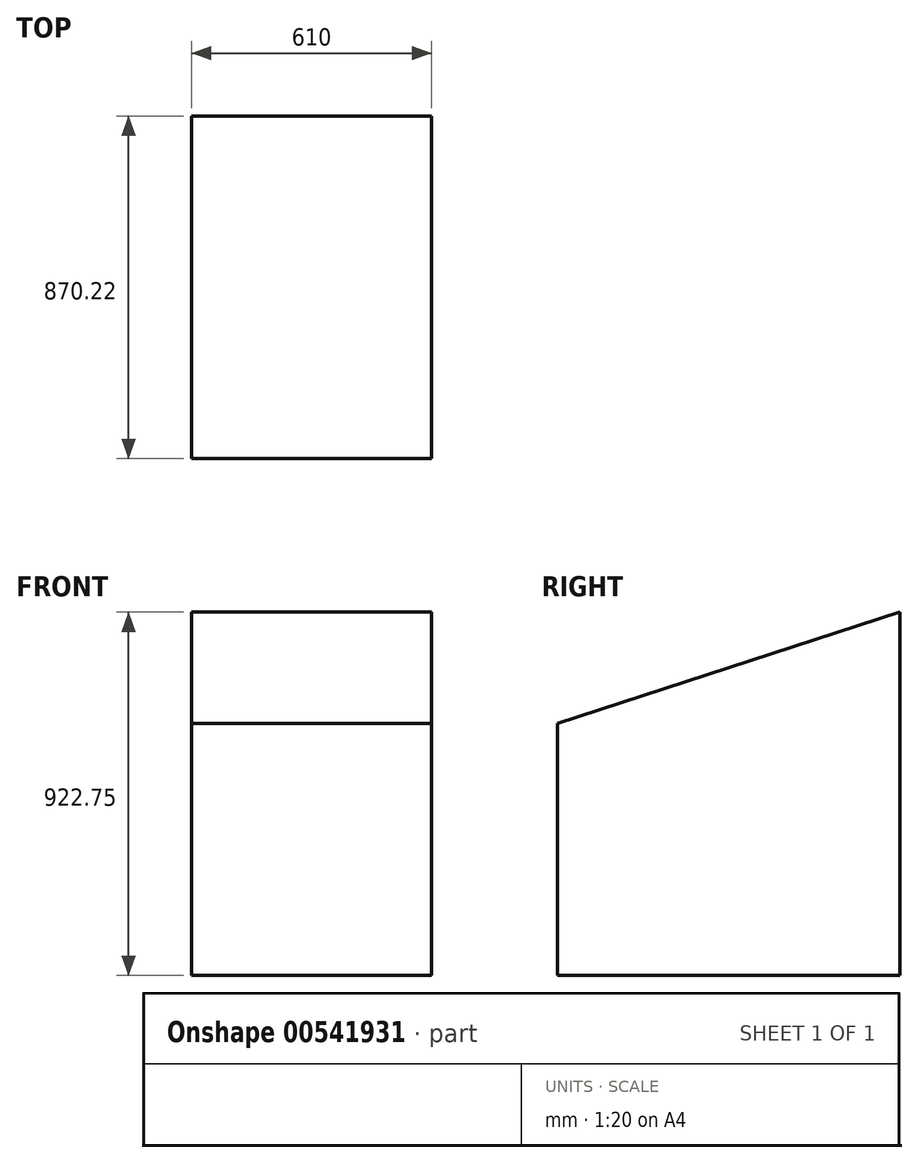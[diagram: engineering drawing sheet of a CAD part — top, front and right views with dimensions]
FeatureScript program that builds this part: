
annotation { "Feature Type Name" : "Feature", "Feature Type Description" : "" }
export const myFeature = defineFeature(function(context is Context, id is Id, definition is map)
    precondition{}
    {
        {
            var Q0;
            Q0=qCreatedBy(makeId("Front.planeOp"),FACE);
            var sketch = newSketch(context, id + "F0", { "sketchPlane" : qUnion([Q0])});
            skLineSegment(sketch, "E0.bottom", {"start": v(-452.22, -343.3) * mm, "end": v(157.78, -343.3) * mm});
            skLineSegment(sketch, "E0.top", {"start": v(-452.22, 296.7) * mm, "end": v(157.78, 296.7) * mm});
            skLineSegment(sketch, "E0.left", {"start": v(-452.22, -343.3) * mm, "end": v(-452.22, 296.7) * mm});
            skLineSegment(sketch, "E0.right", {"start": v(157.78, -343.3) * mm, "end": v(157.78, 296.7) * mm});
            skSolve(sketch);
        }
        {
            var Q0;
            Q0=makeQuery(id+"F0.imprint","IMPRINT",FACE,{"disambiguationData":[TD([[makeQuery(id+"F0.imprint","IMPRINT",EDGE,{"derivedFrom":sQuery(id+"F0.wireOp",EDGE,"E0.bottom")}),1.0]])]});
            var Q1;
            Q1 = qSketchRegion(id + "F2", true);
            extrude(context, id + "F1", {"entities" : qUnion([Q0, Q1]), "depth" : 870.22 * mm, "offsetDistance" : 25.4 * mm});
        }
        {
            var Q0;
            Q0=makeQuery(id+"F1.opExtrude","SWEPT_FACE",FACE,{"disambiguationData":[OSD([sQuery(id+"F0.wireOp",EDGE,"E0.left")])]});
            var sketch = newSketch(context, id + "F2", { "sketchPlane" : qUnion([Q0])});
            skLineSegment(sketch, "E1", {"start": v(870.22, 296.7) * mm, "end": v(0, 579.44) * mm});
            skLineSegment(sketch, "E2", {"start": v(0, 579.44) * mm, "end": v(0, 296.7) * mm});
            skSolve(sketch);
        }
        {
            var Q0;
            Q0=makeQuery(id+"F2.imprint","IMPRINT",FACE,{"disambiguationData":[TD([[makeQuery(id+"F2.imprint","IMPRINT",EDGE,{"derivedFrom":sQuery(id+"F2.wireOp",EDGE,"E1")}),1.0]])]});
            extrude(context, id + "F3", {"entities" : qUnion([Q0]), "operationType" : NewBodyOperationType.ADD, "oppositeDirection" : true, "depth" : 610 * mm, "offsetDistance" : 25.4 * mm});
        }
    });
